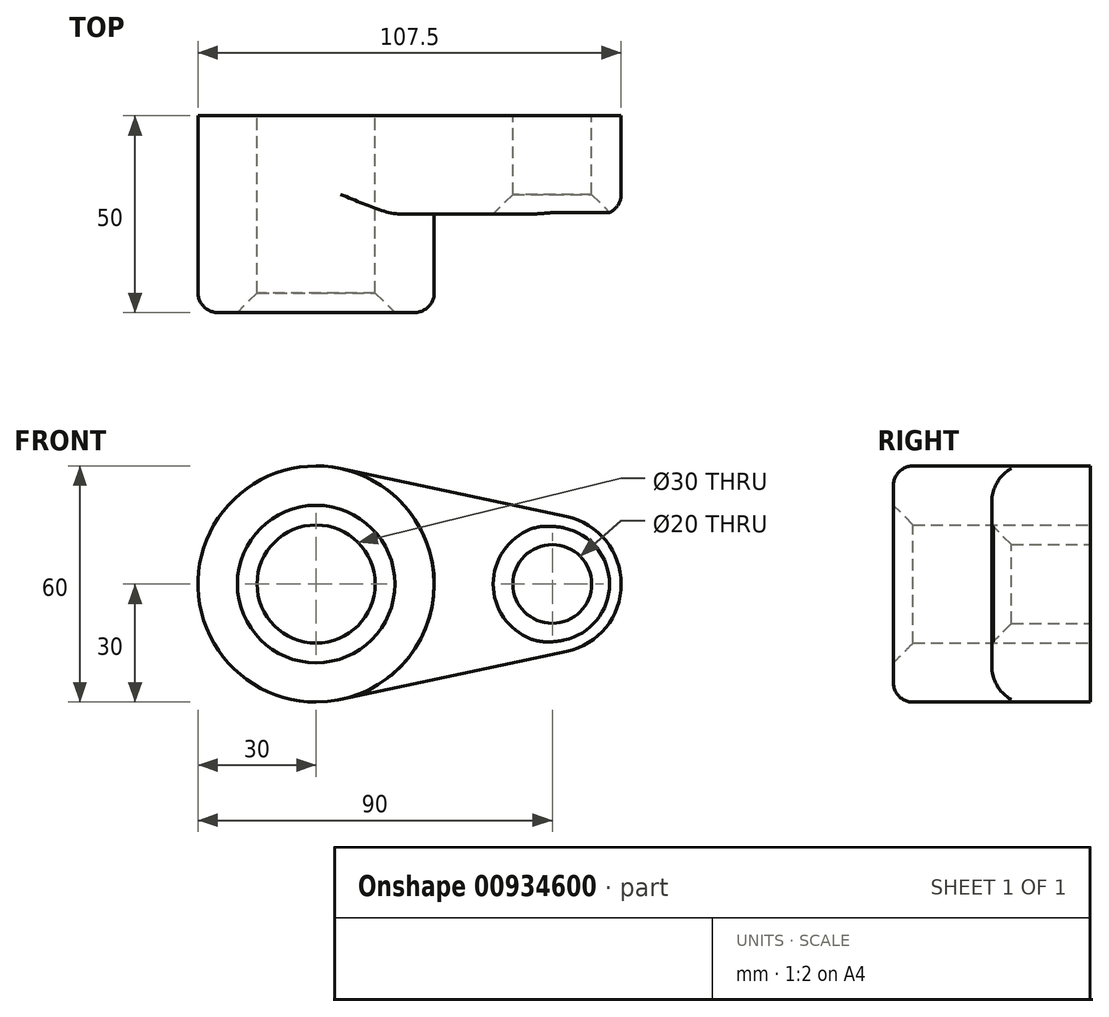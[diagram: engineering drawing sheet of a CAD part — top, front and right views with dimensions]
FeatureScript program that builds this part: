
annotation { "Feature Type Name" : "Feature", "Feature Type Description" : "" }
export const myFeature = defineFeature(function(context is Context, id is Id, definition is map)
    precondition{}
    {
        {
            var Q0;
            Q0=qCreatedBy(makeId("Front.planeOp"),FACE);
            var sketch = newSketch(context, id + "F0", { "sketchPlane" : qUnion([Q0])});
            skCircle(sketch, "E0", {"center": v(0, 0) * mm, "radius": 30 * mm});
            skCircle(sketch, "E1", {"center": v(60, 0) * mm, "radius": 17.5 * mm});
            skLineSegment(sketch, "E2", {"start": v(6.25, 29.34) * mm, "end": v(63.65, 17.12) * mm});
            skLineSegment(sketch, "E3", {"start": v(6.25, -29.34) * mm, "end": v(63.65, -17.12) * mm});
            skCircle(sketch, "E4", {"center": v(0, 0) * mm, "radius": 15 * mm});
            skCircle(sketch, "E5", {"center": v(60, 0) * mm, "radius": 10 * mm});
            skSolve(sketch);
        }
        {
            var Q0;
            Q0 = qSketchRegion(id + "F0", true);
            extrude(context, id + "F1", {"entities" : qUnion([Q0]), "depth" : 25 * mm, "offsetDistance" : 25 * mm});
        }
        {
            var Q0;
            Q0=makeQuery(id+"F0.imprint","IMPRINT",FACE,{"disambiguationData":[TD([[makeQuery(id+"F0.imprint","IMPRINT",EDGE,{"derivedFrom":sQuery(id+"F0.wireOp",EDGE,"E4")}),-1.0]])]});
            extrude(context, id + "F2", {"entities" : qUnion([Q0]), "operationType" : NewBodyOperationType.ADD, "depth" : 50 * mm, "offsetDistance" : 25 * mm});
        }
        {
            var Q0;
            Q0=makeQuery(id+"F2.opExtrude","CAP_EDGE",EDGE,{"disambiguationData":[OSD([sQuery(id+"F0.wireOp",EDGE,"E0")])],"isStart":false});
            var Q1;
            Q1=makeQuery(id+"F1.opExtrude","CAP_EDGE",EDGE,{"disambiguationData":[OSD([sQuery(id+"F0.wireOp",EDGE,"E3")])],"isStart":false});
            var Q2;
            Q2=makeQuery(id+"F1.opExtrude","CAP_EDGE",EDGE,{"disambiguationData":[OSD([sQuery(id+"F0.wireOp",EDGE,"E2")])],"isStart":false});
            var Q3;
            Q3=makeQuery(id+"F1.opExtrude","CAP_EDGE",EDGE,{"disambiguationData":[OSD([sQuery(id+"F0.wireOp",EDGE,"E1")])],"isStart":false});
            fillet(context, id + "F3", {"entities" : qUnion([Q0, Q1, Q2, Q3]), "radius" : 5 * mm, "tangentPropagation" : true, "allowEdgeOverflow" : false});
        }
        {
            var Q0;
            Q0=makeQuery(id+"F2.opExtrude","CAP_EDGE",EDGE,{"disambiguationData":[OSD([sQuery(id+"F0.wireOp",EDGE,"E4")])],"isStart":false});
            var Q1;
            Q1=makeQuery(id+"F1.opExtrude","CAP_EDGE",EDGE,{"disambiguationData":[OSD([sQuery(id+"F0.wireOp",EDGE,"E5")])],"isStart":false});
            chamfer(context, id + "F4", {"entities" : qUnion([Q0, Q1]), "width" : 5 * mm, "tangentPropagation" : true});
        }
    });
